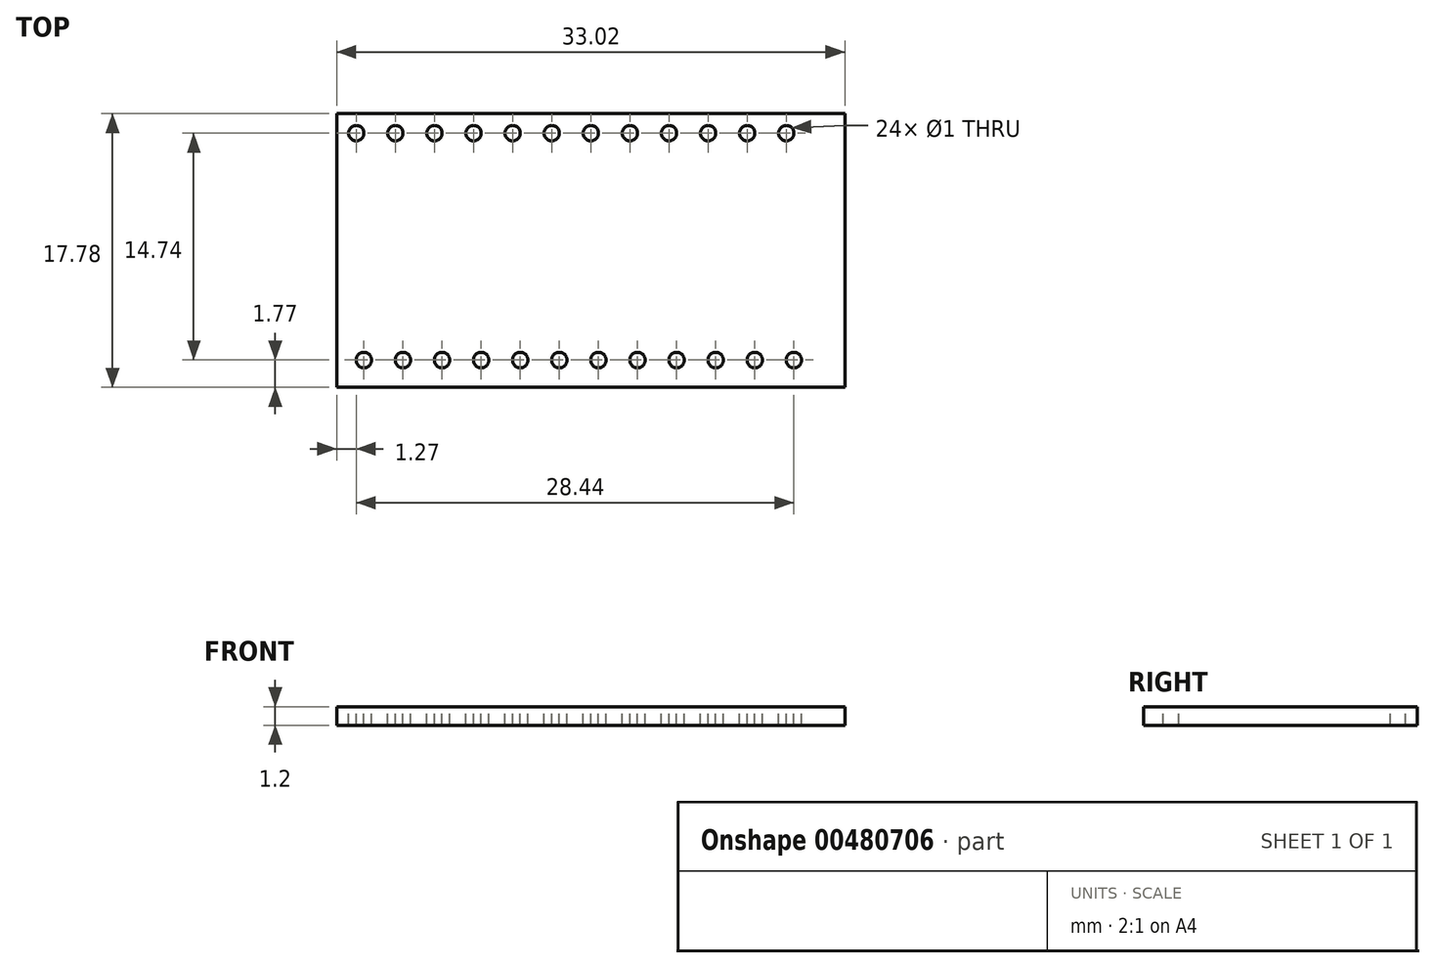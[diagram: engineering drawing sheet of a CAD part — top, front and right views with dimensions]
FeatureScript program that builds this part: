
annotation { "Feature Type Name" : "Feature", "Feature Type Description" : "" }
export const myFeature = defineFeature(function(context is Context, id is Id, definition is map)
    precondition{}
    {
        {
            var Q0;
            Q0=qCreatedBy(makeId("Top.planeOp"),FACE);
            var sketch = newSketch(context, id + "F0", { "sketchPlane" : qUnion([Q0])});
            skLineSegment(sketch, "E0.bottom", {"start": v(0, 0) * mm, "end": v(33.02, 0) * mm});
            skLineSegment(sketch, "E0.top", {"start": v(0, 17.78) * mm, "end": v(33.02, 17.78) * mm});
            skLineSegment(sketch, "E0.left", {"start": v(0, 0) * mm, "end": v(0, 17.78) * mm});
            skLineSegment(sketch, "E0.right", {"start": v(33.02, 0) * mm, "end": v(33.02, 17.78) * mm});
            skSolve(sketch);
        }
        {
            var Q0;
            Q0=makeQuery(id+"F0.imprint","IMPRINT",FACE,{"disambiguationData":[TD([[makeQuery(id+"F0.imprint","IMPRINT",EDGE,{"derivedFrom":sQuery(id+"F0.wireOp",EDGE,"E0.bottom")}),1.0]])]});
            extrude(context, id + "F1", {"entities" : qUnion([Q0]), "depth" : 1.2 * mm});
        }
        {
            var Q0;
            Q0=makeQuery(id+"F1.opExtrude","CAP_FACE",FACE,{"disambiguationData":[OSD([sQuery(id+"F0.wireOp",EDGE,"E0.bottom"),sQuery(id+"F0.wireOp",EDGE,"E0.top"),sQuery(id+"F0.wireOp",EDGE,"E0.left"),sQuery(id+"F0.wireOp",EDGE,"E0.right")])],"isStart":false});
            var sketch = newSketch(context, id + "F2", { "sketchPlane" : qUnion([Q0])});
            skCircle(sketch, "E1", {"center": v(1.77, 1.77) * mm, "radius": 0.5 * mm});
            skCircle(sketch, "E2.1.0.0", {"center": v(4.3, 1.77) * mm, "radius": 0.5 * mm});
            skCircle(sketch, "E2.2.0.0", {"center": v(6.85, 1.77) * mm, "radius": 0.5 * mm});
            skLineSegment(sketch, "E2.direction1", {"start": v(1.77, 1.77) * mm, "end": v(4.3, 1.77) * mm, "construction": true});
            skCircle(sketch, "E3.0.3.0", {"center": v(9.39, 1.77) * mm, "radius": 0.5 * mm});
            skCircle(sketch, "E3.0.4.0", {"center": v(11.93, 1.77) * mm, "radius": 0.5 * mm});
            skCircle(sketch, "E3.0.5.0", {"center": v(14.47, 1.77) * mm, "radius": 0.5 * mm});
            skCircle(sketch, "E3.0.6.0", {"center": v(17, 1.77) * mm, "radius": 0.5 * mm});
            skCircle(sketch, "E3.0.7.0", {"center": v(19.55, 1.77) * mm, "radius": 0.5 * mm});
            skCircle(sketch, "E3.0.8.0", {"center": v(22.09, 1.77) * mm, "radius": 0.5 * mm});
            skCircle(sketch, "E3.0.9.0", {"center": v(24.63, 1.77) * mm, "radius": 0.5 * mm});
            skCircle(sketch, "E3.0.10.0", {"center": v(27.17, 1.77) * mm, "radius": 0.5 * mm});
            skCircle(sketch, "E3.0.11.0", {"center": v(29.7, 1.77) * mm, "radius": 0.5 * mm});
            skCircle(sketch, "E4", {"center": v(1.27, 16.51) * mm, "radius": 0.5 * mm});
            skCircle(sketch, "E5.1.0.0", {"center": v(3.81, 16.51) * mm, "radius": 0.5 * mm});
            skCircle(sketch, "E5.2.0.0", {"center": v(6.35, 16.51) * mm, "radius": 0.5 * mm});
            skCircle(sketch, "E5.3.0.0", {"center": v(8.9, 16.51) * mm, "radius": 0.5 * mm});
            skCircle(sketch, "E5.4.0.0", {"center": v(11.43, 16.51) * mm, "radius": 0.5 * mm});
            skCircle(sketch, "E5.5.0.0", {"center": v(13.97, 16.51) * mm, "radius": 0.5 * mm});
            skCircle(sketch, "E5.6.0.0", {"center": v(16.51, 16.51) * mm, "radius": 0.5 * mm});
            skCircle(sketch, "E5.7.0.0", {"center": v(19.05, 16.51) * mm, "radius": 0.5 * mm});
            skCircle(sketch, "E5.8.0.0", {"center": v(21.6, 16.51) * mm, "radius": 0.5 * mm});
            skCircle(sketch, "E5.9.0.0", {"center": v(24.13, 16.51) * mm, "radius": 0.5 * mm});
            skCircle(sketch, "E5.10.0.0", {"center": v(26.67, 16.51) * mm, "radius": 0.5 * mm});
            skCircle(sketch, "E5.11.0.0", {"center": v(29.21, 16.51) * mm, "radius": 0.5 * mm});
            skLineSegment(sketch, "E5.direction1", {"start": v(1.27, 16.51) * mm, "end": v(3.81, 16.51) * mm, "construction": true});
            skSolve(sketch);
        }
        {
            var Q0;
            Q0=makeQuery(id+"F2.imprint","IMPRINT",FACE,{"disambiguationData":[TD([[makeQuery(id+"F2.imprint","IMPRINT",EDGE,{"derivedFrom":sQuery(id+"F2.wireOp",EDGE,"E4")}),1.0]])]});
            var Q1;
            Q1=makeQuery(id+"F2.imprint","IMPRINT",FACE,{"disambiguationData":[TD([[makeQuery(id+"F2.imprint","IMPRINT",EDGE,{"derivedFrom":sQuery(id+"F2.wireOp",EDGE,"E5.1.0.0")}),1.0]])]});
            var Q2;
            Q2=makeQuery(id+"F2.imprint","IMPRINT",FACE,{"disambiguationData":[TD([[makeQuery(id+"F2.imprint","IMPRINT",EDGE,{"derivedFrom":sQuery(id+"F2.wireOp",EDGE,"E5.2.0.0")}),1.0]])]});
            var Q3;
            Q3=makeQuery(id+"F2.imprint","IMPRINT",FACE,{"disambiguationData":[TD([[makeQuery(id+"F2.imprint","IMPRINT",EDGE,{"derivedFrom":sQuery(id+"F2.wireOp",EDGE,"E5.3.0.0")}),1.0]])]});
            var Q4;
            Q4=makeQuery(id+"F2.imprint","IMPRINT",FACE,{"disambiguationData":[TD([[makeQuery(id+"F2.imprint","IMPRINT",EDGE,{"derivedFrom":sQuery(id+"F2.wireOp",EDGE,"E5.4.0.0")}),1.0]])]});
            var Q5;
            Q5=makeQuery(id+"F2.imprint","IMPRINT",FACE,{"disambiguationData":[TD([[makeQuery(id+"F2.imprint","IMPRINT",EDGE,{"derivedFrom":sQuery(id+"F2.wireOp",EDGE,"E5.5.0.0")}),1.0]])]});
            var Q6;
            Q6=makeQuery(id+"F2.imprint","IMPRINT",FACE,{"disambiguationData":[TD([[makeQuery(id+"F2.imprint","IMPRINT",EDGE,{"derivedFrom":sQuery(id+"F2.wireOp",EDGE,"E5.6.0.0")}),1.0]])]});
            var Q7;
            Q7=makeQuery(id+"F2.imprint","IMPRINT",FACE,{"disambiguationData":[TD([[makeQuery(id+"F2.imprint","IMPRINT",EDGE,{"derivedFrom":sQuery(id+"F2.wireOp",EDGE,"E5.7.0.0")}),1.0]])]});
            var Q8;
            Q8=makeQuery(id+"F2.imprint","IMPRINT",FACE,{"disambiguationData":[TD([[makeQuery(id+"F2.imprint","IMPRINT",EDGE,{"derivedFrom":sQuery(id+"F2.wireOp",EDGE,"E5.8.0.0")}),1.0]])]});
            var Q9;
            Q9=makeQuery(id+"F2.imprint","IMPRINT",FACE,{"disambiguationData":[TD([[makeQuery(id+"F2.imprint","IMPRINT",EDGE,{"derivedFrom":sQuery(id+"F2.wireOp",EDGE,"E5.9.0.0")}),1.0]])]});
            var Q10;
            Q10=makeQuery(id+"F2.imprint","IMPRINT",FACE,{"disambiguationData":[TD([[makeQuery(id+"F2.imprint","IMPRINT",EDGE,{"derivedFrom":sQuery(id+"F2.wireOp",EDGE,"E5.10.0.0")}),1.0]])]});
            var Q11;
            Q11=makeQuery(id+"F2.imprint","IMPRINT",FACE,{"disambiguationData":[TD([[makeQuery(id+"F2.imprint","IMPRINT",EDGE,{"derivedFrom":sQuery(id+"F2.wireOp",EDGE,"E5.11.0.0")}),1.0]])]});
            var Q12;
            Q12=makeQuery(id+"F2.imprint","IMPRINT",FACE,{"disambiguationData":[TD([[makeQuery(id+"F2.imprint","IMPRINT",EDGE,{"derivedFrom":sQuery(id+"F2.wireOp",EDGE,"E3.0.11.0")}),1.0]])]});
            var Q13;
            Q13=makeQuery(id+"F2.imprint","IMPRINT",FACE,{"disambiguationData":[TD([[makeQuery(id+"F2.imprint","IMPRINT",EDGE,{"derivedFrom":sQuery(id+"F2.wireOp",EDGE,"E3.0.10.0")}),1.0]])]});
            var Q14;
            Q14=makeQuery(id+"F2.imprint","IMPRINT",FACE,{"disambiguationData":[TD([[makeQuery(id+"F2.imprint","IMPRINT",EDGE,{"derivedFrom":sQuery(id+"F2.wireOp",EDGE,"E3.0.9.0")}),1.0]])]});
            var Q15;
            Q15=makeQuery(id+"F2.imprint","IMPRINT",FACE,{"disambiguationData":[TD([[makeQuery(id+"F2.imprint","IMPRINT",EDGE,{"derivedFrom":sQuery(id+"F2.wireOp",EDGE,"E3.0.8.0")}),1.0]])]});
            var Q16;
            Q16=makeQuery(id+"F2.imprint","IMPRINT",FACE,{"disambiguationData":[TD([[makeQuery(id+"F2.imprint","IMPRINT",EDGE,{"derivedFrom":sQuery(id+"F2.wireOp",EDGE,"E3.0.7.0")}),1.0]])]});
            var Q17;
            Q17=makeQuery(id+"F2.imprint","IMPRINT",FACE,{"disambiguationData":[TD([[makeQuery(id+"F2.imprint","IMPRINT",EDGE,{"derivedFrom":sQuery(id+"F2.wireOp",EDGE,"E3.0.6.0")}),1.0]])]});
            var Q18;
            Q18=makeQuery(id+"F2.imprint","IMPRINT",FACE,{"disambiguationData":[TD([[makeQuery(id+"F2.imprint","IMPRINT",EDGE,{"derivedFrom":sQuery(id+"F2.wireOp",EDGE,"E3.0.5.0")}),1.0]])]});
            var Q19;
            Q19=makeQuery(id+"F2.imprint","IMPRINT",FACE,{"disambiguationData":[TD([[makeQuery(id+"F2.imprint","IMPRINT",EDGE,{"derivedFrom":sQuery(id+"F2.wireOp",EDGE,"E3.0.4.0")}),1.0]])]});
            var Q20;
            Q20=makeQuery(id+"F2.imprint","IMPRINT",FACE,{"disambiguationData":[TD([[makeQuery(id+"F2.imprint","IMPRINT",EDGE,{"derivedFrom":sQuery(id+"F2.wireOp",EDGE,"E3.0.3.0")}),1.0]])]});
            var Q21;
            Q21=makeQuery(id+"F2.imprint","IMPRINT",FACE,{"disambiguationData":[TD([[makeQuery(id+"F2.imprint","IMPRINT",EDGE,{"derivedFrom":sQuery(id+"F2.wireOp",EDGE,"E2.2.0.0")}),1.0]])]});
            var Q22;
            Q22=makeQuery(id+"F2.imprint","IMPRINT",FACE,{"disambiguationData":[TD([[makeQuery(id+"F2.imprint","IMPRINT",EDGE,{"derivedFrom":sQuery(id+"F2.wireOp",EDGE,"E2.1.0.0")}),1.0]])]});
            var Q23;
            Q23=makeQuery(id+"F2.imprint","IMPRINT",FACE,{"disambiguationData":[TD([[makeQuery(id+"F2.imprint","IMPRINT",EDGE,{"derivedFrom":sQuery(id+"F2.wireOp",EDGE,"E1")}),1.0]])]});
            extrude(context, id + "F3", {"entities" : qUnion([Q0, Q1, Q2, Q3, Q4, Q5, Q6, Q7, Q8, Q9, Q10, Q11, Q12, Q13, Q14, Q15, Q16, Q17, Q18, Q19, Q20, Q21, Q22, Q23]), "operationType" : NewBodyOperationType.REMOVE, "endBound" : BoundingType.THROUGH_ALL, "oppositeDirection" : true, "depth" : 25.4 * mm});
        }
    });
